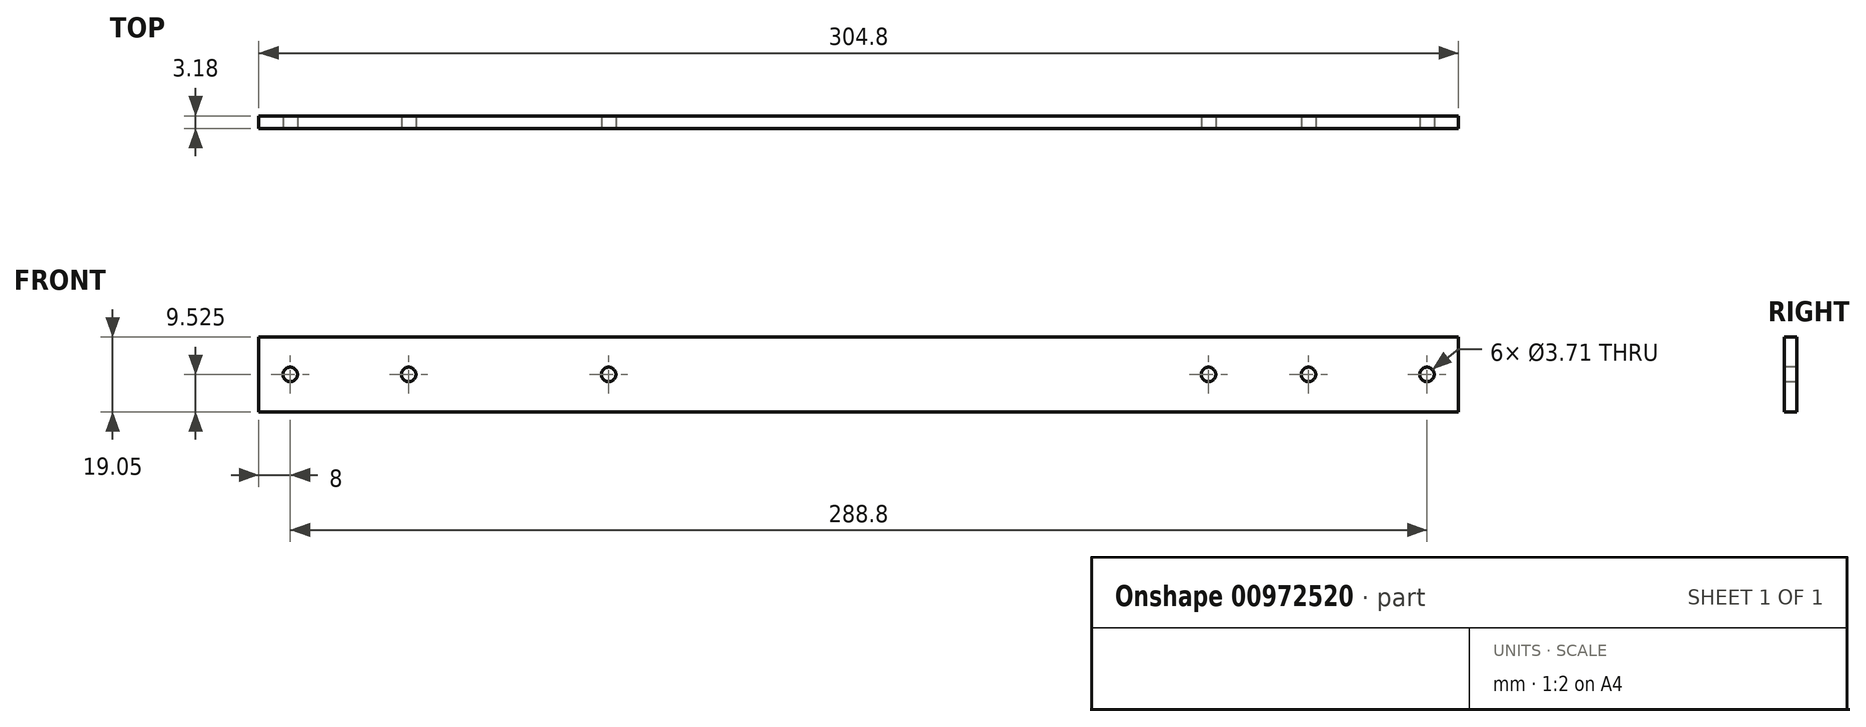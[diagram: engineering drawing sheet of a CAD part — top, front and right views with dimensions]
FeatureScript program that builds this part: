
annotation { "Feature Type Name" : "Feature", "Feature Type Description" : "" }
export const myFeature = defineFeature(function(context is Context, id is Id, definition is map)
    precondition{}
    {
        {
            var Q0;
            Q0=qCreatedBy(makeId("Front.planeOp"),FACE);
            var sketch = newSketch(context, id + "F0", { "sketchPlane" : qUnion([Q0])});
            skLineSegment(sketch, "E0.bottom", {"start": v(0, 0) * mm, "end": v(-304.8, 0) * mm});
            skLineSegment(sketch, "E0.top", {"start": v(0, 19.05) * mm, "end": v(-304.8, 19.05) * mm});
            skLineSegment(sketch, "E0.left", {"start": v(0, 0) * mm, "end": v(0, 19.05) * mm});
            skLineSegment(sketch, "E0.right", {"start": v(-304.8, 0) * mm, "end": v(-304.8, 19.05) * mm});
            skSolve(sketch);
        }
        {
            var Q0;
            Q0=makeQuery(id+"F0.imprint","IMPRINT",FACE,{"disambiguationData":[TD([[makeQuery(id+"F0.imprint","IMPRINT",EDGE,{"derivedFrom":sQuery(id+"F0.wireOp",EDGE,"E0.bottom")}),-1.0]])]});
            extrude(context, id + "F1", {"entities" : qUnion([Q0]), "depth" : 3.17 * mm, "offsetDistance" : 25.4 * mm});
        }
        {
            var Q0;
            Q0=makeQuery(id+"F1.opExtrude","CAP_FACE",FACE,{"disambiguationData":[OSD([sQuery(id+"F0.wireOp",EDGE,"E0.bottom"),sQuery(id+"F0.wireOp",EDGE,"E0.top"),sQuery(id+"F0.wireOp",EDGE,"E0.left"),sQuery(id+"F0.wireOp",EDGE,"E0.right")])],"isStart":false});
            var sketch = newSketch(context, id + "F2", { "sketchPlane" : qUnion([Q0])});
            skCircle(sketch, "E1", {"center": v(-296.8, 9.52) * mm, "radius": 1.86 * mm});
            skPoint(sketch, "E1.centerSnap0", {"position": v(-304.8, 9.52) * mm});
            skCircle(sketch, "E2", {"center": v(-266.7, 9.52) * mm, "radius": 1.86 * mm});
            skCircle(sketch, "E3", {"center": v(-215.9, 9.52) * mm, "radius": 1.86 * mm});
            skCircle(sketch, "E4", {"center": v(-63.5, 9.53) * mm, "radius": 1.86 * mm});
            skCircle(sketch, "E5", {"center": v(-38.1, 9.53) * mm, "radius": 1.86 * mm});
            skCircle(sketch, "E6", {"center": v(-8, 9.53) * mm, "radius": 1.86 * mm});
            skSolve(sketch);
        }
        {
            var Q0;
            Q0 = qSketchRegion(id + "F2", true);
            extrude(context, id + "F3", {"entities" : qUnion([Q0]), "operationType" : NewBodyOperationType.REMOVE, "oppositeDirection" : true, "depth" : 25.4 * mm, "offsetDistance" : 25.4 * mm});
        }
    });
